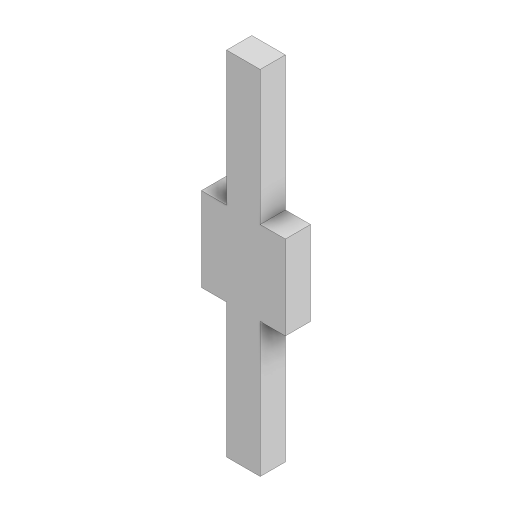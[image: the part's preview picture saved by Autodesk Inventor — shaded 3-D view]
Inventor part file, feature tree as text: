
AUTODESK INVENTOR PART (.ipt)
format: ipt  version: 2023.3 (Build 273359000, 359)  size: 103,936 bytes
history: native  units: mm
features: extrude x1, sketch x1
ambient origin geometry x8: Origin, YZ Plane, XZ Plane, XY Plane, X Axis, Y Axis, Z Axis, Center Point
bodies: Solid1 (feature_tree)
feature tree (2):
  extrude  "Extrusion1"  Depth=10.0mm
  sketch  "Sketch1"  dims[d0=48.0mm d1=10.0mm d2=3.0mm d3=10.0mm d4=4.0mm d5=3.0mm d6=3.0mm d7=0.0mm]
